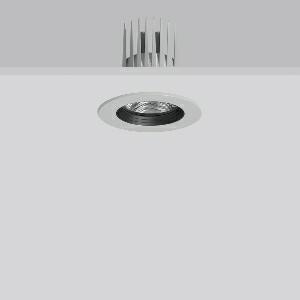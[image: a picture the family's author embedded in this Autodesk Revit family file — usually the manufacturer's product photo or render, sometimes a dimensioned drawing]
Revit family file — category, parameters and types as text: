
# Revit family: heledon_mini_e_901741_004_2_a7d5
name_source: partatom
category: Lighting Fixtures
units: mm (PartAtom-declared; Revit-internal decimal feet)

## family parameters
Cut with Voids When Loaded = No
Host = Face
Light Source = No
Part Type = Normal
Room Calculation Point = No
Round Connector Dimension = Use Diameter
Shared = No

## types (1)
- HELEDON mini E (1 x LED Modul 927, 2300 lm, 2700)
    Apparent Load = 20 VA
    Approval mark = CE
    CIE Flux Codes = 99 100 100 100 100
    Color Rendering = 92
    Color Temperature = 2700
    Default Elevation = 1800 mm
    Description = Series: HELEDON mini
Round recessed downlight. Housing: die-cast aluminium, powder-coated. Black plastic ring and recessed LED to prevent glare from the side. Optical assembly with reflector made of MIRO-Silver with 98% total light reflection for outstanding efficiency - can be changed without tools. Best colour rendering index Ra>90. Suitable for Recessed ceiling mounting. Installation without tools thanks to spring fastening system. Including separate LED converter with connecting cable 600 mm.High quality converter without flickering and stroboscopic effect. Through-wiring box (5 pole) available as accessory. The following accessories can be mounted without use of tools: interchangeable lenses, decorative glasses, honeycomb louvre, clear and frosted diffusers, white interchangeable plastic ring. 
Colour: silver
Diameter: 124 mm
Height: 3 mm
Cut-out diameter: 114 mm
Recess height: 170 mm
Luminaire: recess height: 120 mm
Lamp: LED
Socket: without socket
Colour temperature: 2700K
Colour rendering index (CRI): 92
System power: 20 W
Rated luminous flux: 2300 lm
Luminous efficiency: 115 lm/W
Control gear: Regulated power supply
Protection class: II
Type of protection: IP 20
    Height = 0 mm  [stored 0 ft]
    Lamp = 1 x LED Modul 927
    Lamp Light Flux = 2300 lm
    Lamp count = 1
    Length = 124 mm  [stored 0.406824 ft]
    Lifetime = 50000 h
    Luminous efficacy = 115 lm/W
    Manufacturer = RZB
    ModVariant = No
    Model = 901741.004.2
    Mounting Place = Ceiling
    Mounting Type = Recessed
    Number of Poles = 1
    OnlyDefault = Yes
    Power Factor = 1
    Product Name = HELEDON mini E
    Product group = Recessed downlights
    ProductGroupID = 402
    Protection Class = Protection class II
    Protection Degree = IP 20
    RLX_Detail_Level = 1
    RLX_Emergency_Light_Flux = 0 lm
    RLX_Emergency_Type = 0
    RLX_Emergency_Type_DB = No
    RlxData = <blob elided: 130789 chars, md5=3444061d>
    Socket = socket
    Standby Power = 0 W
    System Light Flux = 2300 lm
    System Power = 20 W
    Type Comments = Product without accessories
    Type Image = 901657.004.jpg
    URL = http://relux.com
    VarID = ---
    Voltage = 230 V
    Voltage Range = 220-240 V
    Weight = 0.00 kg
    Width = 0 mm  [stored 0 ft]

note: [stored X ft] marks values corroborated as IEEE doubles in the binary element streams (Revit-internal decimal feet)

## geometry (parser evidence)
native form markers: Blend x4, Sweep x9
no freeform markers — native parametric forms only
